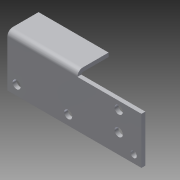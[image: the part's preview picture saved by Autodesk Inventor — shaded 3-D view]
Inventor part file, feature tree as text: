
AUTODESK INVENTOR PART (.ipt)
format: ipt  version: 2013 (Build 170138000, 138)  size: 194,560 bytes
history: native  units: in
note: dims shown in document units (in); Inventor stores cm internally (conversion verified against a paired STEP export)
features: sketch x7, other x6, sheet_metal_op x4, reference x4, extrude x1
ambient origin geometry x8: Origin, YZ Plane, XZ Plane, XY Plane, X Axis, Y Axis, Z Axis, Center Point
bodies: Solid1 (feature_tree)
feature tree (22):
  sheet_metal_op  "Face1"
  sheet_metal_op  "Flange1"
  sketch  "Sketch9"  dims[d5=0.295in]
  extrude  "Extrusion1"  Depth=1.5in
  sketch  "Sketch1"  dims[d1=2.244in d2=1.5in]
  other  "Plate1"
  sketch  "Sketch2"  dims[d3=0.295in]
  other  "Plate2"
  sheet_metal_op  "Bend1"
  sheet_metal_op  "Corner1"
  sketch  "Sketch8"  dims[d4=1.181in]
  reference  "Reference1"
  reference  "Reference2"
  sketch  "Sketch10"  dims[d8=0.125in]
  sketch  "Sketch12"  dims[d9=0.125in]
  reference  "Reference5"
  reference  "Reference6"
  sketch  "Sketch13"  dims[d10=0.0625in d11=0.25in d12=0.125in d13=1.0in d14=90.0deg d15=0.05in d16=0.5in d17=0.125in d18=0.125in d19=0.125in d20=0.0in d21=2.053in d22=0.0in d25=0.125in d26=0.0in d27=0.25in d28=0.25in d29=0.2in d30=0.125in d31=0.0in d0=0.0625in d6=0.0in]
  other  "Cut1"
  other  "Cut3"
  other  "Cut4"
  other  "Definition1"
